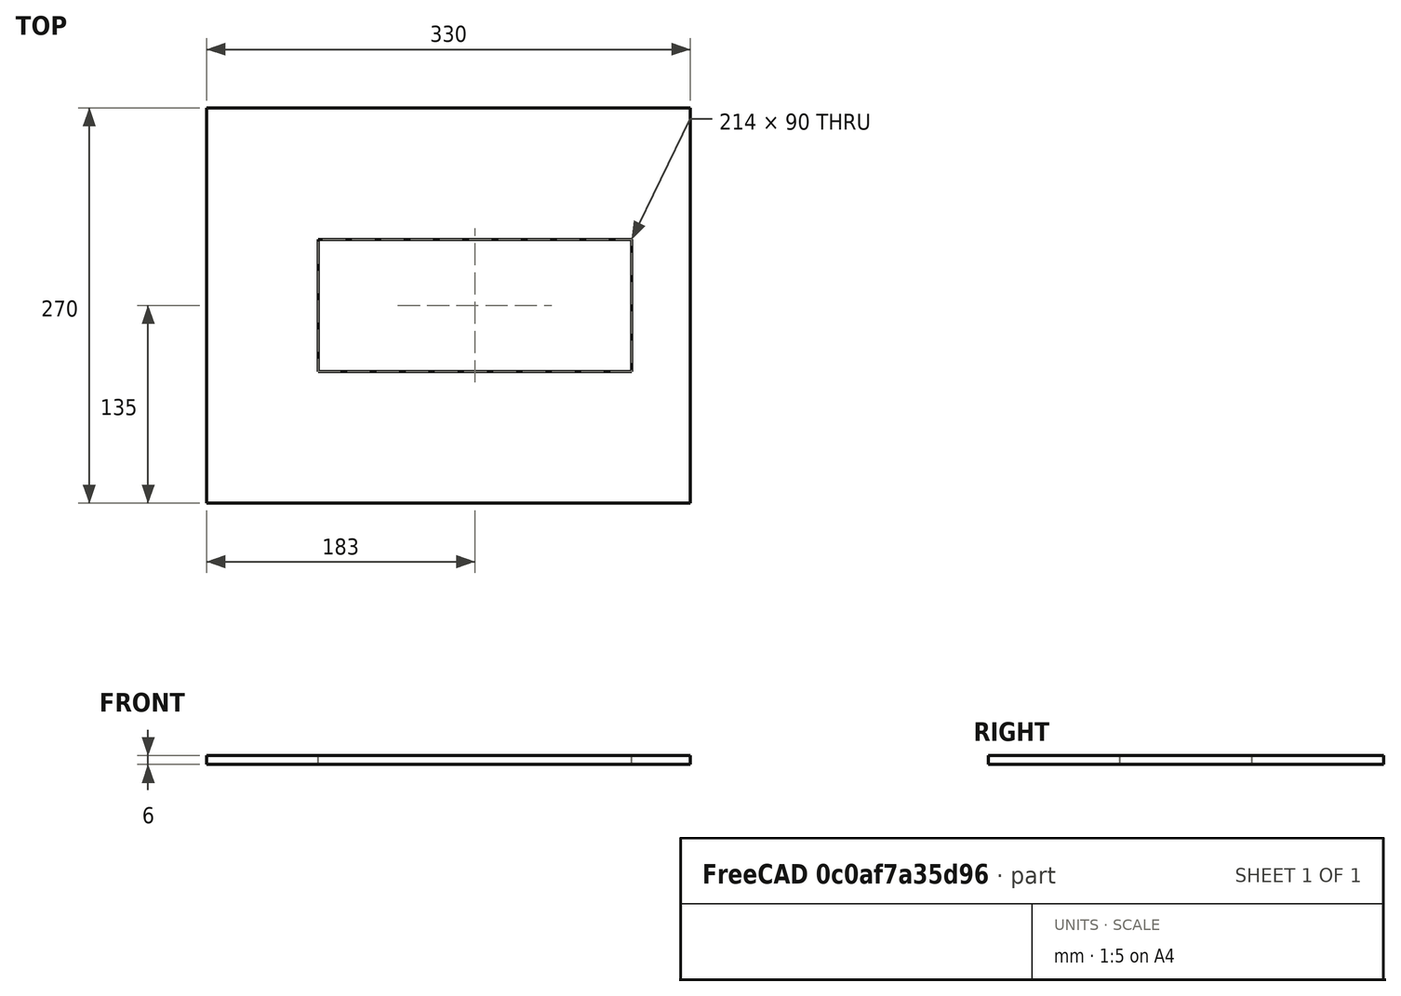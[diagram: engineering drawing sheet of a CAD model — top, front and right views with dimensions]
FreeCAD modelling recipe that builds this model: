
FCSTD DOCUMENT  (FreeCAD 0.18R4 (GitTag))
Label: cubierta_husillos
License: All rights reserved
LicenseURL: http://en.wikipedia.org/wiki/All_rights_reserved
objects: Sketcher::SketchObject×1, PartDesign::Pad×1, PartDesign::Body×1
note: 4 computed .brp shape members not serialized (recipe doc carries the construction recipe); baked Part::Feature solids carry a one-line shape summary decoded from their .brp

FEATURE [Sketcher::SketchObject] Sketch
  MapMode = 5
  Support = -> [XY_Plane]
  sketch-geometry (8):
    g0: LineSegment StartX=0 StartY=0 StartZ=0 EndX=330 EndY=0 EndZ=0
    g1: LineSegment StartX=330 StartY=0 StartZ=0 EndX=330 EndY=270 EndZ=0
    g2: LineSegment StartX=330 StartY=270 StartZ=0 EndX=0 EndY=270 EndZ=0
    g3: LineSegment StartX=0 StartY=270 StartZ=0 EndX=0 EndY=0 EndZ=0
    g4: LineSegment StartX=76 StartY=180 StartZ=0 EndX=290 EndY=180 EndZ=0
    g5: LineSegment StartX=290 StartY=180 StartZ=0 EndX=290 EndY=90 EndZ=0
    g6: LineSegment StartX=290 StartY=90 StartZ=0 EndX=76 EndY=90 EndZ=0
    g7: LineSegment StartX=76 StartY=90 StartZ=0 EndX=76 EndY=180 EndZ=0
  constraints (23):
    c: Coincident(g0,g1)
    c: Coincident(g1,g2)
    c: Coincident(g2,g3)
    c: Coincident(g3,g0)
    c: Horizontal(g0)
    c: Horizontal(g2)
    c: Vertical(g1)
    c: Vertical(g3)
    c: DistanceX(g0,g0) = 330
    c: Coincident(g0,g-1)
    c: DistanceY(g3,g3) = 270
    c: Coincident(g4,g5)
    c: Coincident(g5,g6)
    c: Coincident(g6,g7)
    c: Coincident(g7,g4)
    c: Horizontal(g4)
    c: Horizontal(g6)
    c: Vertical(g5)
    c: Vertical(g7)
    c: Distance(g4,g3) = 76
    c: Distance(g4,g1) = 40
    c: Distance(g6,g0) = 90
    c: Distance(g4,g2) = 90
FEATURE [PartDesign::Pad] Pad
  Length = 6
  Length2 = 100
  Profile = -> Sketch
  Type = 0
FEATURE [PartDesign::Body] Body
  Group = -> [Sketch,Pad]
  Origin = -> Origin
  Tip = -> Pad
